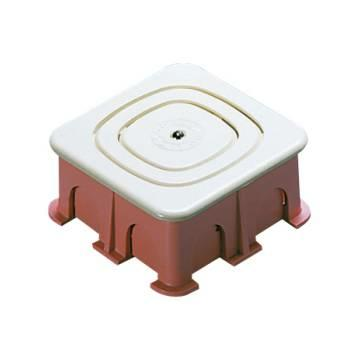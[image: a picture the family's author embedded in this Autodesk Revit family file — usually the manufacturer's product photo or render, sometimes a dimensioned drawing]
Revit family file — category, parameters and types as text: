
# Revit family: Building-FlushMountingEnclosures-GEWISS-24SC-BOXES_PHONE_SYSTEM
name_source: partatom
category: Apparecchi elettrici
revit_build: Autodesk Revit 2016 (Build: 20161004_0715(x64)
units: mm (PartAtom-declared; Revit-internal decimal feet)

## family parameters
Condiviso = Sì
Host = Muro
Mantenere orientamento annotazione = Sì
Numero OmniClass = 23.80.30.14.24
Punto di calcolo locali = Sì
Quota connettore circolare = Usa diametro
Sempre verticale = Sì
Taglio con vuoti quando caricato = Sì
Tipo di parte = Normale
Titolo OmniClass = Junction Boxes

## types (1)
- GW24221 - Telecom standard box
    Catalogue = BUILDING
    Catalogue Range = 24SC
    Descrizione = TELECOM CONVEN.STD.BOX
    EAN code = 8011564016644
    Electrocod = 0210
    For walls = Masonry
    IDF = 6a44e20c-771d-4a70-ba3f-b58bcbd83a3d
    IDT = 72fbfc7d-f9ad-4603-970f-2f3f2820655a
    Immagine tipo = GW24221.jpg
    Installation = Flush mounting enclosures
    Lid colour = Ivory
    Modello = GW24221
    Outer dim. LxHxD (mm) = 68x68x30
    Produttore = GEWISS S.p.A.
    SEO = Box
    Technical sheet = https://www.gewiss.com
    Type of installation = Conventional
    URL = https://www.gewiss.com
    Version file RFA = 19.0
